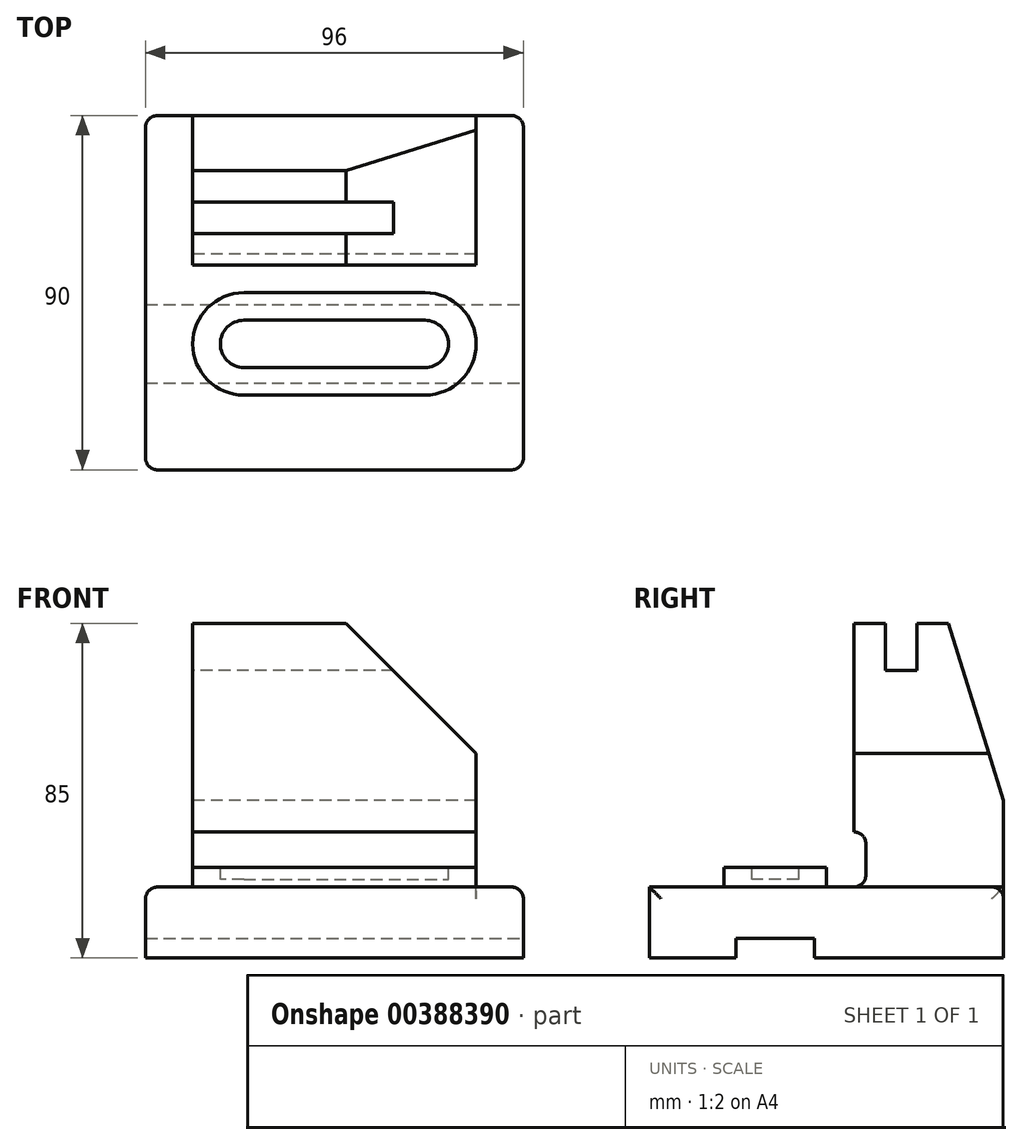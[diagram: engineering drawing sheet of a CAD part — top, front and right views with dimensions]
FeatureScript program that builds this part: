
annotation { "Feature Type Name" : "Feature", "Feature Type Description" : "" }
export const myFeature = defineFeature(function(context is Context, id is Id, definition is map)
    precondition{}
    {
        {
            var Q0;
            Q0=qCreatedBy(makeId("Top.planeOp"),FACE);
            var sketch = newSketch(context, id + "F0", { "sketchPlane" : qUnion([Q0])});
            skLineSegment(sketch, "E0.bottom", {"start": v(0, 0) * mm, "end": v(96, 0) * mm});
            skLineSegment(sketch, "E0.top", {"start": v(0, 90) * mm, "end": v(96, 90) * mm});
            skLineSegment(sketch, "E0.left", {"start": v(0, 0) * mm, "end": v(0, 90) * mm});
            skLineSegment(sketch, "E0.right", {"start": v(96, 0) * mm, "end": v(96, 90) * mm});
            skSolve(sketch);
        }
        {
            var Q0;
            Q0 = qSketchRegion(id + "F0", true);
            extrude(context, id + "F1", {"entities" : qUnion([Q0]), "depth" : 18 * mm});
        }
        {
            var Q0;
            Q0=makeQuery(id+"F1.opExtrude","CAP_FACE",FACE,{"disambiguationData":[OSD([sQuery(id+"F0.wireOp",EDGE,"E0.bottom"),sQuery(id+"F0.wireOp",EDGE,"E0.top"),sQuery(id+"F0.wireOp",EDGE,"E0.left"),sQuery(id+"F0.wireOp",EDGE,"E0.right")])],"isStart":false});
            var sketch = newSketch(context, id + "F2", { "sketchPlane" : qUnion([Q0])});
            skLineSegment(sketch, "E1.bottom", {"start": v(12, 90) * mm, "end": v(84, 90) * mm});
            skLineSegment(sketch, "E1.top", {"start": v(12, 52) * mm, "end": v(84, 52) * mm});
            skLineSegment(sketch, "E1.left", {"start": v(12, 90) * mm, "end": v(12, 52) * mm});
            skLineSegment(sketch, "E1.right", {"start": v(84, 90) * mm, "end": v(84, 52) * mm});
            skSolve(sketch);
        }
        {
            var Q0;
            Q0=makeQuery(id+"F1.opExtrude","CAP_FACE",FACE,{"disambiguationData":[OSD([sQuery(id+"F0.wireOp",EDGE,"E0.bottom"),sQuery(id+"F0.wireOp",EDGE,"E0.top"),sQuery(id+"F0.wireOp",EDGE,"E0.left"),sQuery(id+"F0.wireOp",EDGE,"E0.right")])],"isStart":true});
            cPlane(context, id + "F3", {"entities" : qUnion([Q0]), "cplaneType" : CPlaneType.OFFSET, "offset" : 85 * mm, "oppositeDirection" : true, "width" : 150 * mm, "height" : 150 * mm});
        }
        {
            var Q0;
            Q0 = qSketchRegion(id + "F2", true);
            var Q1;
            Q1=qCreatedBy(id+"F3.planeOp",FACE);
            extrude(context, id + "F4", {"entities" : qUnion([Q0]), "operationType" : NewBodyOperationType.ADD, "endBound" : BoundingType.UP_TO_SURFACE, "endBoundEntityFace" : qUnion([Q1]), "depth" : 58 * mm});
        }
        {
            var Q0;
            Q0=makeQuery(id+"F4.opExtrude","SWEPT_FACE",FACE,{"disambiguationData":[OSD([sQuery(id+"F2.wireOp",EDGE,"E1.top")])]});
            var sketch = newSketch(context, id + "F5", { "sketchPlane" : qUnion([Q0])});
            skLineSegment(sketch, "E2", {"start": v(84, 85) * mm, "end": v(51, 85) * mm});
            skLineSegment(sketch, "E3", {"start": v(51, 85) * mm, "end": v(84, 52) * mm});
            skSolve(sketch);
        }
        {
            var Q0;
            {var subQ0=sQuery(id+"F5.wireOp",EDGE,"E2");Q0=makeQuery(id+"F5.imprint","IMPRINT",FACE,{"disambiguationData":[TD([[makeQuery(id+"F5.imprint","IMPRINT",EDGE,{"derivedFrom":subQ0}),1.0]])]});}
            extrude(context, id + "F6", {"entities" : qUnion([Q0]), "operationType" : NewBodyOperationType.REMOVE, "oppositeDirection" : true, "depth" : 38 * mm});
        }
        {
            var Q0;
            Q0=makeQuery(id+"F4.opExtrude","SWEPT_FACE",FACE,{"disambiguationData":[OSD([sQuery(id+"F2.wireOp",EDGE,"E1.left")])]});
            var sketch = newSketch(context, id + "F7", { "sketchPlane" : qUnion([Q0])});
            skLineSegment(sketch, "E4.bottom", {"start": v(-60, 85) * mm, "end": v(-68, 85) * mm});
            skLineSegment(sketch, "E4.top", {"start": v(-60, 73) * mm, "end": v(-68, 73) * mm});
            skLineSegment(sketch, "E4.left", {"start": v(-60, 85) * mm, "end": v(-60, 73) * mm});
            skLineSegment(sketch, "E4.right", {"start": v(-68, 85) * mm, "end": v(-68, 73) * mm});
            skSolve(sketch);
        }
        {
            var Q0;
            Q0=makeQuery(id+"F7.imprint","IMPRINT",FACE,{"disambiguationData":[TD([[makeQuery(id+"F7.imprint","IMPRINT",EDGE,{"derivedFrom":sQuery(id+"F7.wireOp",EDGE,"E4.bottom")}),1.0]])]});
            extrude(context, id + "F8", {"entities" : qUnion([Q0]), "operationType" : NewBodyOperationType.REMOVE, "endBound" : BoundingType.UP_TO_NEXT, "oppositeDirection" : true, "depth" : 25 * mm});
        }
        {
            var Q0;
            Q0=makeQuery(id+"F4.opExtrude","SWEPT_FACE",FACE,{"disambiguationData":[OSD([sQuery(id+"F2.wireOp",EDGE,"E1.left")])]});
            var sketch = newSketch(context, id + "F9", { "sketchPlane" : qUnion([Q0])});
            skLineSegment(sketch, "E5", {"start": v(-90, 85) * mm, "end": v(-76, 85) * mm});
            skLineSegment(sketch, "E6", {"start": v(-76, 85) * mm, "end": v(-90, 40) * mm});
            skSolve(sketch);
        }
        {
            var Q0;
            {var subQ0=sQuery(id+"F9.wireOp",EDGE,"E5");Q0=makeQuery(id+"F9.imprint","IMPRINT",FACE,{"disambiguationData":[TD([[makeQuery(id+"F9.imprint","IMPRINT",EDGE,{"derivedFrom":subQ0}),1.0]])]});}
            extrude(context, id + "F10", {"entities" : qUnion([Q0]), "operationType" : NewBodyOperationType.REMOVE, "endBound" : BoundingType.UP_TO_NEXT, "oppositeDirection" : true, "depth" : 25 * mm});
        }
        {
            var Q0;
            Q0=makeQuery(id+"F1.opExtrude","SWEPT_FACE",FACE,{"disambiguationData":[OSD([sQuery(id+"F0.wireOp",EDGE,"E0.right")])]});
            var sketch = newSketch(context, id + "F11", { "sketchPlane" : qUnion([Q0])});
            skLineSegment(sketch, "E7.bottom", {"start": v(22, 0) * mm, "end": v(42, 0) * mm});
            skLineSegment(sketch, "E7.top", {"start": v(22, 5) * mm, "end": v(42, 5) * mm});
            skLineSegment(sketch, "E7.left", {"start": v(22, 0) * mm, "end": v(22, 5) * mm});
            skLineSegment(sketch, "E7.right", {"start": v(42, 0) * mm, "end": v(42, 5) * mm});
            skPoint(sketch, "E8", {"position": v(32, 5) * mm});
            skSolve(sketch);
        }
        {
            var Q0;
            Q0=makeQuery(id+"F11.imprint","IMPRINT",FACE,{"disambiguationData":[TD([[makeQuery(id+"F11.imprint","IMPRINT",EDGE,{"derivedFrom":sQuery(id+"F11.wireOp",EDGE,"E7.bottom")}),1.0]])]});
            extrude(context, id + "F12", {"entities" : qUnion([Q0]), "operationType" : NewBodyOperationType.REMOVE, "endBound" : BoundingType.UP_TO_NEXT, "oppositeDirection" : true, "depth" : 25 * mm});
        }
        {
            var Q0;
            Q0=makeQuery(id+"F1.opExtrude","CAP_FACE",FACE,{"disambiguationData":[OSD([sQuery(id+"F0.wireOp",EDGE,"E0.bottom"),sQuery(id+"F0.wireOp",EDGE,"E0.top"),sQuery(id+"F0.wireOp",EDGE,"E0.left"),sQuery(id+"F0.wireOp",EDGE,"E0.right")])],"isStart":false});
            var sketch = newSketch(context, id + "F13", { "sketchPlane" : qUnion([Q0])});
            skLineSegment(sketch, "E9.bottom", {"start": v(25, 45) * mm, "end": v(71, 45) * mm});
            skLineSegment(sketch, "E9.top", {"start": v(25, 19) * mm, "end": v(71, 19) * mm});
            skLineSegment(sketch, "E9.left", {"start": v(25, 45) * mm, "end": v(25, 19) * mm});
            skLineSegment(sketch, "E9.right", {"start": v(71, 45) * mm, "end": v(71, 19) * mm});
            skLineSegment(sketch, "E10", {"start": v(25, 32) * mm, "end": v(71, 32) * mm, "construction": true});
            skArc(sketch, "E11", {"start": v(25, 19) * mm, "mid": v(12, 32) * mm, "end": v(25, 45) * mm});
            skArc(sketch, "E12", {"start": v(71, 19) * mm, "mid": v(84, 32) * mm, "end": v(71, 45) * mm});
            skSolve(sketch);
        }
        {
            var Q0;
            Q0 = qSketchRegion(id + "F13", true);
            extrude(context, id + "F14", {"entities" : qUnion([Q0]), "operationType" : NewBodyOperationType.ADD, "depth" : 5 * mm});
        }
        {
            var Q0;
            Q0=makeQuery(id+"F14.opExtrude","CAP_FACE",FACE,{"disambiguationData":[OSD([sQuery(id+"F13.wireOp",EDGE,"E9.bottom"),sQuery(id+"F13.wireOp",EDGE,"E9.top"),sQuery(id+"F13.wireOp",EDGE,"E11"),sQuery(id+"F13.wireOp",EDGE,"E12")])],"isStart":false});
            var sketch = newSketch(context, id + "F15", { "sketchPlane" : qUnion([Q0])});
            skLineSegment(sketch, "E13.JeR.JeR", {"start": v(25, 32) * mm, "end": v(71, 32) * mm, "construction": true});
            skArc(sketch, "E13.0.startCap", {"start": v(25, 26) * mm, "mid": v(19, 32) * mm, "end": v(25, 38) * mm});
            skArc(sketch, "E13.0.endCap", {"start": v(71, 38) * mm, "mid": v(77, 32) * mm, "end": v(71, 26) * mm});
            skLineSegment(sketch, "E13.0.left", {"start": v(25, 38) * mm, "end": v(71, 38) * mm});
            skLineSegment(sketch, "E13.0.right", {"start": v(25, 26) * mm, "end": v(71, 26) * mm});
            skSolve(sketch);
        }
        {
            var Q0;
            Q0 = qSketchRegion(id + "F15", true);
            extrude(context, id + "F16", {"entities" : qUnion([Q0]), "operationType" : NewBodyOperationType.REMOVE, "oppositeDirection" : true, "depth" : 3 * mm});
        }
        {
            var Q0;
            Q0=makeQuery(id+"F4.opExtrude","SWEPT_FACE",FACE,{"disambiguationData":[OSD([sQuery(id+"F2.wireOp",EDGE,"E1.right")])]});
            var sketch = newSketch(context, id + "F17", { "sketchPlane" : qUnion([Q0])});
            skLineSegment(sketch, "E14.bottom", {"start": v(52, 18) * mm, "end": v(55, 18) * mm});
            skLineSegment(sketch, "E14.top", {"start": v(52, 32) * mm, "end": v(55, 32) * mm});
            skLineSegment(sketch, "E14.left", {"start": v(52, 18) * mm, "end": v(52, 32) * mm});
            skLineSegment(sketch, "E14.right", {"start": v(55, 18) * mm, "end": v(55, 32) * mm});
            skSolve(sketch);
        }
        {
            var Q0;
            Q0=makeQuery(id+"F17.imprint","IMPRINT",FACE,{"disambiguationData":[TD([[makeQuery(id+"F17.imprint","IMPRINT",EDGE,{"derivedFrom":sQuery(id+"F17.wireOp",EDGE,"E14.bottom")}),-1.0]])]});
            extrude(context, id + "F18", {"entities" : qUnion([Q0]), "operationType" : NewBodyOperationType.REMOVE, "endBound" : BoundingType.UP_TO_NEXT, "oppositeDirection" : true, "depth" : 25 * mm});
        }
        {
            var Q0;
            Q0=makeQuery(id+"F14.opExtrude","CAP_EDGE",EDGE,{"disambiguationData":[OSD([sQuery(id+"F13.wireOp",EDGE,"E9.top")])],"isStart":true});
            var Q1;
            Q1=makeQuery(id+"F18.boolean.opBoolean","COPY",EDGE,{"derivedFrom":makeQuery(id+"F18.opExtrude","SWEPT_EDGE",EDGE,{"disambiguationData":[OSD([sQuery(id+"F2.wireOp",EDGE,"E1.right"),sQuery(id+"F17.wireOp",EDGE,"E14.bottom"),sQuery(id+"F17.wireOp",EDGE,"E14.right")])]})});
            var Q2;
            Q2=makeQuery(id+"F18.boolean.opBoolean","COPY",EDGE,{"derivedFrom":makeQuery(id+"F18.opExtrude","SWEPT_EDGE",EDGE,{"disambiguationData":[OSD([sQuery(id+"F17.wireOp",EDGE,"E14.top"),sQuery(id+"F17.wireOp",EDGE,"E14.right")])]})});
            var Q3;
            {var subQ0=sQuery(id+"F0.wireOp",EDGE,"E0.right");var subQ1=sQuery(id+"F0.wireOp",EDGE,"E0.top");Q3=makeQuery(id+"F4.boolean.opBoolean","SPLIT",EDGE,{"disambiguationData":[TD([makeQuery(id+"F1.opExtrude","SWEPT_FACE",FACE,{"disambiguationData":[OSD([subQ0])]})])],"derivedFrom":makeQuery(id+"F1.opExtrude","CAP_EDGE",EDGE,{"disambiguationData":[OSD([subQ1])],"isStart":false})});}
            var Q4;
            Q4=makeQuery(id+"F1.opExtrude","SWEPT_EDGE",EDGE,{"disambiguationData":[OSD([sQuery(id+"F0.wireOp",EDGE,"E0.bottom"),sQuery(id+"F0.wireOp",EDGE,"E0.right")])]});
            var Q5;
            Q5=makeQuery(id+"F1.opExtrude","SWEPT_EDGE",EDGE,{"disambiguationData":[OSD([sQuery(id+"F0.wireOp",EDGE,"E0.top"),sQuery(id+"F0.wireOp",EDGE,"E0.right")])]});
            var Q6;
            Q6=makeQuery(id+"F1.opExtrude","SWEPT_EDGE",EDGE,{"disambiguationData":[OSD([sQuery(id+"F0.wireOp",EDGE,"E0.top"),sQuery(id+"F0.wireOp",EDGE,"E0.left")])]});
            var Q7;
            Q7=makeQuery(id+"F1.opExtrude","SWEPT_EDGE",EDGE,{"disambiguationData":[OSD([sQuery(id+"F0.wireOp",EDGE,"E0.bottom"),sQuery(id+"F0.wireOp",EDGE,"E0.left")])]});
            var Q8;
            Q8=makeQuery(id+"F1.opExtrude","CAP_EDGE",EDGE,{"disambiguationData":[OSD([sQuery(id+"F0.wireOp",EDGE,"E0.left")])],"isStart":false});
            var Q9;
            Q9=makeQuery(id+"F1.opExtrude","CAP_EDGE",EDGE,{"disambiguationData":[OSD([sQuery(id+"F0.wireOp",EDGE,"E0.right")])],"isStart":false});
            var Q10;
            Q10=makeQuery(id+"F4.opExtrude","CAP_EDGE",EDGE,{"disambiguationData":[OSD([sQuery(id+"F2.wireOp",EDGE,"E1.right")])],"isStart":true});
            fillet(context, id + "F19", {"entities" : qUnion([Q0, Q1, Q2, Q3, Q4, Q5, Q6, Q7, Q8, Q9, Q10]), "radius" : 3 * mm, "tangentPropagation" : true, "allowEdgeOverflow" : false});
        }
    });
